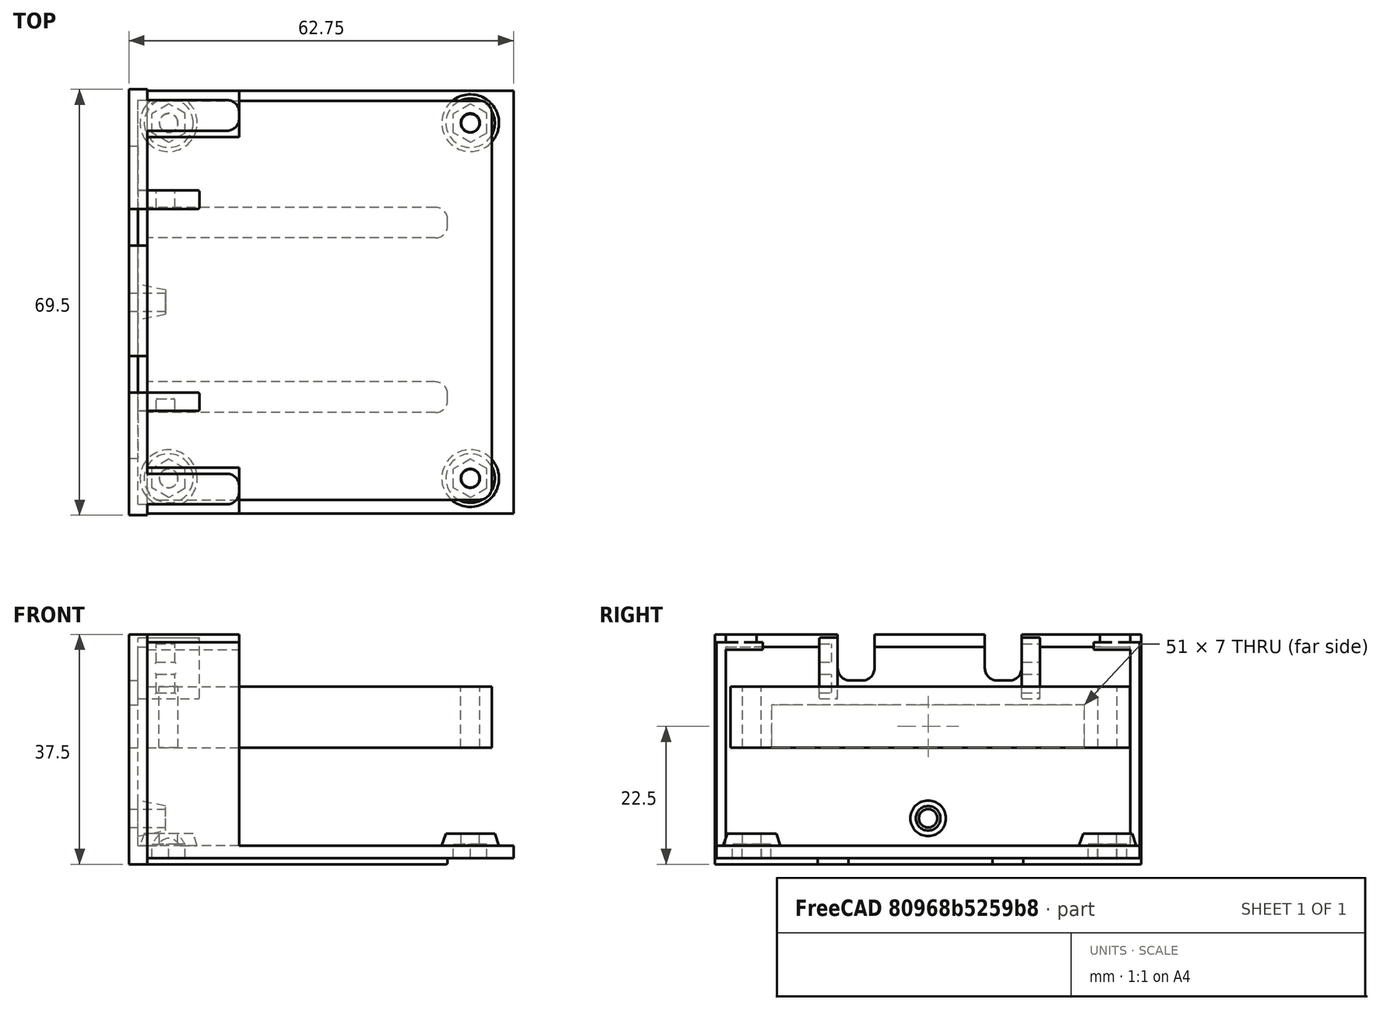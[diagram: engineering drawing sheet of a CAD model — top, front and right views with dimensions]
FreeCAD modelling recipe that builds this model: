
FCSTD DOCUMENT  (FreeCAD 0.19R24291 (Git))
Label: relay_tray
License: All rights reserved
LicenseURL: http://en.wikipedia.org/wiki/All_rights_reserved
objects: Part::Box×45, Part::MultiFuse×27, Part::Fillet×13, Part::Cut×10, Part::Cylinder×10, Part::Cone×6, Part::MultiCommon×4
note: 115 computed .brp shape members not serialized (recipe doc carries the construction recipe); baked Part::Feature solids carry a one-line shape summary decoded from their .brp

FEATURE [Part::Box] Box001  label="Cube"
  AttacherType = Attacher::AttachEngine3D
  Height = 37.5
  Length = 3
  Placement = pos=(-3,0,0) rot=(0,0,1;0rad)
  Width = 69.5
FEATURE [Part::Box] Box002  label="Cube001"
  AttacherType = Attacher::AttachEngine3D
  Height = 2
  Length = 60
  Placement = pos=(-0.25,0.25,1) rot=(0,0,1;0rad)
  Width = 69
FEATURE [Part::Box] Box003  label="Cube002"
  AttacherType = Attacher::AttachEngine3D
  Height = 34.75
  Length = 15
  Placement = pos=(0,0,2) rot=(0,0,1;0rad)
  Width = 7.5
FEATURE [Part::Box] Box004  label="Cube003"
  AttacherType = Attacher::AttachEngine3D
  Height = 34.75
  Length = 15
  Placement = pos=(0,61.5,2) rot=(0,0,1;0rad)
  Width = 7.5
FEATURE [Part::Box] Box005  label="Cube004"
  AttacherType = Attacher::AttachEngine3D
  Height = 34
  Length = 15
  Placement = pos=(0,1.5,1) rot=(0,0,1;0rad)
  Width = 7.5
FEATURE [Part::Box] Box006  label="Cube005"
  AttacherType = Attacher::AttachEngine3D
  Height = 34
  Length = 15
  Placement = pos=(0,60,1) rot=(0,0,1;0rad)
  Width = 7.5
FEATURE [Part::MultiFuse] Fusion001
  Shapes = -> [Box006,Box005]
FEATURE [Part::MultiFuse] Fusion002
  Placement = pos=(0,0,-0.5) rot=(0,0,1;0rad)
  Shapes = -> [Box004,Box003]
FEATURE [Part::Cut] Cut001
  Base = -> Fusion002
  Placement = pos=(0,0.25,0) rot=(0,0,1;0rad)
  Tool = -> Fusion001
FEATURE [Part::Box] Box007  label="Cube006"
  AttacherType = Attacher::AttachEngine3D
  Height = 32.5
  Length = 3.5
  Placement = pos=(-1.5,1.75,3) rot=(0,0,1;0rad)
  Width = 66
FEATURE [Part::Cut] Cut002
  Base = -> Box001
  Tool = -> Box007
FEATURE [Part::Cylinder] Cylinder004
  Angle = 360
  AttacherType = Attacher::AttachEngine3D
  Height = 10
  Placement = pos=(-5,6,32.5) rot=(0,1,0;1.5708rad)
  Radius = 1.5
FEATURE [Part::Cylinder] Cylinder005
  Angle = 360
  AttacherType = Attacher::AttachEngine3D
  Height = 10
  Placement = pos=(-5,6,32.5) rot=(0,1,0;1.5708rad)
  Radius = 1.5
FEATURE [Part::MultiFuse] Fusion003
  Placement = pos=(0,28.75,-25) rot=(0,0,1;0rad)
  Shapes = -> [Cylinder004,Cylinder005]
  expr: .Placement.Base.z = -25
FEATURE [Part::Box] Box008  label="Cube007"
  AttacherType = Attacher::AttachEngine3D
  Height = 7
  Length = 10
  Placement = pos=(-5,9.25,19) rot=(0,0,1;0rad)
  Width = 51
FEATURE [Part::Cone] Cone
  Angle = 360
  AttacherType = Attacher::AttachEngine3D
  Height = 5
  Placement = pos=(-1,6,32.5) rot=(0,1,0;1.5708rad)
  Radius1 = 3
  Radius2 = 2
FEATURE [Part::Cone] Cone001
  Angle = 360
  AttacherType = Attacher::AttachEngine3D
  Height = 5
  Placement = pos=(-1,6,32.5) rot=(0,1,0;1.5708rad)
  Radius1 = 3
  Radius2 = 2
FEATURE [Part::MultiFuse] Fusion004
  Placement = pos=(-1,28.75,-25) rot=(0,0,1;0rad)
  Shapes = -> [Cone,Cone001]
  expr: .Placement.Base.z = -25
FEATURE [Part::MultiFuse] Fusion005
  Shapes = -> [Cut002,Fusion004]
FEATURE [Part::Cut] Cut003
  Base = -> Fusion005
  Tool = -> Fusion003
FEATURE [Part::Cut] Cut004
  Base = -> Cut003
  Tool = -> Box008
FEATURE [Part::Cone] Cone002
  Angle = 360
  AttacherType = Attacher::AttachEngine3D
  Height = 3
  Placement = pos=(3.5,3.5,2) rot=(0,0,1;0rad)
  Radius1 = 5
  Radius2 = 4
FEATURE [Part::Box] Box014  label="Cube014"
  AttacherType = Attacher::AttachEngine3D
  Height = 5
  Length = 5.45
  Placement = pos=(3.25,0,0) rot=(0,0,1;0rad)
  Width = 10
FEATURE [Part::Box] Box015  label="Cube015"
  AttacherType = Attacher::AttachEngine3D
  Height = 5
  Length = 5.45
  Placement = pos=(11.5,4,0) rot=(0,0,1;2.0944rad)
  Width = 10
FEATURE [Part::Box] Box016  label="Cube016"
  AttacherType = Attacher::AttachEngine3D
  Height = 5
  Length = 10
  Placement = pos=(0.55,4,0) rot=(0,0,-1;0.523599rad)
  Width = 5.45
FEATURE [Part::Cylinder] Cylinder006
  Angle = 360
  AttacherType = Attacher::AttachEngine3D
  Height = 10
  Placement = pos=(4,4,-1) rot=(0,0,1;0rad)
  Radius = 1.5
FEATURE [Part::MultiCommon] Common  label="M.25 nut"
  Placement = pos=(-2,0,-1) rot=(0,0,1;0rad)
  Shapes = -> [Box014,Box016,Box015]
FEATURE [Part::MultiFuse] Fusion008  label="screw_hole"
  Placement = pos=(-0.5,-0.5,0) rot=(0,0,1;0rad)
  Shapes = -> [Cylinder006,Common]
FEATURE [Part::Cone] Cone003
  Angle = 360
  AttacherType = Attacher::AttachEngine3D
  Height = 3
  Placement = pos=(3.5,61.52,2) rot=(0,0,1;0rad)
  Radius1 = 5
  Radius2 = 4
FEATURE [Part::Cone] Cone004
  Angle = 360
  AttacherType = Attacher::AttachEngine3D
  Height = 3
  Placement = pos=(52.71,3.5,2) rot=(0,0,1;0rad)
  Radius1 = 5
  Radius2 = 4
FEATURE [Part::Cone] Cone005
  Angle = 360
  AttacherType = Attacher::AttachEngine3D
  Height = 3
  Placement = pos=(52.71,61.52,2) rot=(0,0,1;0rad)
  Radius1 = 5
  Radius2 = 4
FEATURE [Part::Box] Box017  label="Cube017"
  AttacherType = Attacher::AttachEngine3D
  Height = 5
  Length = 5.45
  Placement = pos=(3.25,0,0) rot=(0,0,1;0rad)
  Width = 10
FEATURE [Part::Box] Box018  label="Cube018"
  AttacherType = Attacher::AttachEngine3D
  Height = 5
  Length = 5.45
  Placement = pos=(11.5,4,0) rot=(0,0,1;2.0944rad)
  Width = 10
FEATURE [Part::Cylinder] Cylinder007
  Angle = 360
  AttacherType = Attacher::AttachEngine3D
  Height = 10
  Placement = pos=(4,4,-1) rot=(0,0,1;0rad)
  Radius = 1.5
FEATURE [Part::Box] Box019  label="Cube019"
  AttacherType = Attacher::AttachEngine3D
  Height = 5
  Length = 10
  Placement = pos=(0.55,4,0) rot=(0,0,-1;0.523599rad)
  Width = 5.45
FEATURE [Part::MultiCommon] Common001  label="M.25 nut001"
  Placement = pos=(-2,0,-1) rot=(0,0,1;0rad)
  Shapes = -> [Box017,Box019,Box018]
FEATURE [Part::MultiFuse] Fusion009  label="screw_hole001"
  Placement = pos=(-0.5,57.5,0) rot=(0,0,1;0rad)
  Shapes = -> [Cylinder007,Common001]
FEATURE [Part::Box] Box020  label="Cube020"
  AttacherType = Attacher::AttachEngine3D
  Height = 5
  Length = 5.45
  Placement = pos=(3.25,0,0) rot=(0,0,1;0rad)
  Width = 10
FEATURE [Part::Box] Box021  label="Cube021"
  AttacherType = Attacher::AttachEngine3D
  Height = 5
  Length = 5.45
  Placement = pos=(11.5,4,0) rot=(0,0,1;2.0944rad)
  Width = 10
FEATURE [Part::Cylinder] Cylinder008
  Angle = 360
  AttacherType = Attacher::AttachEngine3D
  Height = 10
  Placement = pos=(4,4,-1) rot=(0,0,1;0rad)
  Radius = 1.5
FEATURE [Part::Box] Box022  label="Cube022"
  AttacherType = Attacher::AttachEngine3D
  Height = 5
  Length = 10
  Placement = pos=(0.55,4,0) rot=(0,0,-1;0.523599rad)
  Width = 5.45
FEATURE [Part::MultiCommon] Common002  label="M.25 nut002"
  Placement = pos=(-2,0,-1) rot=(0,0,1;0rad)
  Shapes = -> [Box020,Box022,Box021]
FEATURE [Part::MultiFuse] Fusion010  label="screw_hole002"
  Placement = pos=(48.71,-0.5,0) rot=(0,0,1;0rad)
  Shapes = -> [Cylinder008,Common002]
FEATURE [Part::Box] Box023  label="Cube023"
  AttacherType = Attacher::AttachEngine3D
  Height = 5
  Length = 5.45
  Placement = pos=(3.25,0,0) rot=(0,0,1;0rad)
  Width = 10
FEATURE [Part::Box] Box024  label="Cube024"
  AttacherType = Attacher::AttachEngine3D
  Height = 5
  Length = 5.45
  Placement = pos=(11.5,4,0) rot=(0,0,1;2.0944rad)
  Width = 10
FEATURE [Part::Cylinder] Cylinder009
  Angle = 360
  AttacherType = Attacher::AttachEngine3D
  Height = 10
  Placement = pos=(4,4,-1) rot=(0,0,1;0rad)
  Radius = 1.5
FEATURE [Part::Box] Box025  label="Cube025"
  AttacherType = Attacher::AttachEngine3D
  Height = 5
  Length = 10
  Placement = pos=(0.55,4,0) rot=(0,0,-1;0.523599rad)
  Width = 5.45
FEATURE [Part::MultiCommon] Common003  label="M.25 nut003"
  Placement = pos=(-2,0,-1) rot=(0,0,1;0rad)
  Shapes = -> [Box023,Box025,Box024]
FEATURE [Part::MultiFuse] Fusion011  label="screw_hole003"
  Placement = pos=(48.71,57.5,0) rot=(0,0,1;0rad)
  Shapes = -> [Cylinder009,Common003]
FEATURE [Part::MultiFuse] Fusion012  label="Screw holes cut"
  Placement = pos=(0,2.5,-0.7) rot=(0,0,1;0rad)
  Shapes = -> [Fusion008,Fusion009,Fusion010,Fusion011]
FEATURE [Part::MultiFuse] Fusion013  label="Cones"
  Placement = pos=(0,2.5,0) rot=(0,0,1;0rad)
  Shapes = -> [Cone002,Cone003,Cone004,Cone005]
FEATURE [Part::MultiFuse] Fusion014
  Shapes = -> [Fusion013,Cut004,Box002]
FEATURE [Part::Cut] Cut005
  Base = -> Fusion014
  Tool = -> Fusion012
FEATURE [Part::Box] Box026  label="Cube026"
  AttacherType = Attacher::AttachEngine3D
  Height = 15
  Length = 10
  Placement = pos=(0,0,16) rot=(0,0,1;0rad)
  Width = 6
FEATURE [Part::Fillet] Fillet012
  Base = -> Box026
  Edges = 2 edges r=2: [Edge9,Edge11]
  Placement = pos=(-4,20,7) rot=(0,0,1;0rad)
FEATURE [Part::Box] Box027  label="Cube027"
  AttacherType = Attacher::AttachEngine3D
  Height = 15
  Length = 10
  Placement = pos=(0,0,16) rot=(0,0,1;0rad)
  Width = 6
FEATURE [Part::Fillet] Fillet013
  Base = -> Box027
  Edges = 2 edges r=2: [Edge9,Edge11]
  Placement = pos=(-4,44,7) rot=(0,0,1;0rad)
FEATURE [Part::MultiFuse] Fusion016  label="Cables sockets"
  Placement = pos=(0,0,7) rot=(0,0,1;0rad)
  Shapes = -> [Fillet012,Fillet013]
FEATURE [Part::Box] Box028  label="Cube028"
  AttacherType = Attacher::AttachEngine3D
  Height = 2
  Length = 15
  Placement = pos=(0,-15.5,0) rot=(0,0,1;0rad)
  Width = 5
FEATURE [Part::Fillet] Fillet
  Base = -> Box028
  Edges = 2 edges r=2: [Edge5,Edge7]
  Placement = pos=(0,17,0) rot=(0,0,1;0rad)
FEATURE [Part::Box] Box029  label="Cube029"
  AttacherType = Attacher::AttachEngine3D
  Height = 2
  Length = 49
  Width = 5
FEATURE [Part::Fillet] Fillet014
  Base = -> Box029
  Edges = 2 edges r=2: [Edge5,Edge7]
  Placement = pos=(0,45,0) rot=(0,0,1;0rad)
FEATURE [Part::Fillet] Fillet015
  Base = -> Fillet
  Edges = 2 edges r=0.25: [Edge14,Edge16]
  Placement = pos=(0,0.25,35.5) rot=(0,0,1;0rad)
FEATURE [Part::Fillet] Fillet016
  Base = -> Fillet014
  Edges = 2 edges r=0.25: [Edge14,Edge16]
  Placement = pos=(0,0.25,0) rot=(0,0,1;0rad)
FEATURE [Part::Box] Box030  label="Cube030"
  AttacherType = Attacher::AttachEngine3D
  Height = 2
  Length = 49
  Width = 5
FEATURE [Part::Fillet] Fillet017
  Base = -> Box030
  Edges = 2 edges r=2: [Edge5,Edge7]
  Placement = pos=(0,17,0) rot=(0,0,1;0rad)
FEATURE [Part::Fillet] Fillet018
  Base = -> Fillet017
  Edges = 2 edges r=0.25: [Edge14,Edge16]
  Placement = pos=(0,-0.25,0) rot=(0,0,1;0rad)
FEATURE [Part::Box] Box031  label="Cube031"
  AttacherType = Attacher::AttachEngine3D
  Height = 2
  Length = 15
  Placement = pos=(0,-15.25,0) rot=(0,0,1;0rad)
  Width = 5
FEATURE [Part::Fillet] Fillet019
  Base = -> Box031
  Edges = 2 edges r=2: [Edge5,Edge7]
  Placement = pos=(0,17,0) rot=(0,0,1;0rad)
FEATURE [Part::Fillet] Fillet020
  Base = -> Fillet019
  Edges = 2 edges r=0.25: [Edge14,Edge16]
  Placement = pos=(0,61,35.5) rot=(0,0,1;0rad)
FEATURE [Part::MultiFuse] Fusion017  label="rails"
  Shapes = -> [Fillet015,Fillet016,Fillet018,Fillet020]
FEATURE [Part::MultiFuse] Fusion018  label="Arduino tray rough"
  Shapes = -> [Fusion017]
FEATURE [Part::Box] Box032  label="Cube032"
  AttacherType = Attacher::AttachEngine3D
  Height = 10
  Length = 10
  Placement = pos=(0,10,26) rot=(0,0,1;0rad)
  Width = 3
FEATURE [Part::Box] Box033  label="Cube033"
  AttacherType = Attacher::AttachEngine3D
  Height = 3
  Length = 3
  Placement = pos=(3,10,27) rot=(0,0,1;0rad)
  Width = 2
FEATURE [Part::Box] Box034  label="Cube034"
  AttacherType = Attacher::AttachEngine3D
  Height = 3
  Length = 3
  Placement = pos=(3,10,32) rot=(0,0,1;0rad)
  Width = 2
FEATURE [Part::MultiFuse] Fusion019
  Shapes = -> [Box033,Box034]
FEATURE [Part::Cut] Cut007
  Base = -> Box032
  Tool = -> Fusion019
FEATURE [Part::Fillet] Fillet022  label="zip ties holder"
  Base = -> Cut007
  Edges = 22 edges r=0.2: [Edge5,Edge6,Edge7,Edge8,Edge9,Edge10,Edge11,Edge12,Edge13,Edge14,Edge15,Edge16,Edge19,Edge20,Edge21,Edge22,Edge23,Edge24,Edge25,Edge26,Edge27,Edge28]
  Placement = pos=(-1,0,-1) rot=(0,0,1;0rad)
FEATURE [Part::Box] Box035  label="Cube035"
  AttacherType = Attacher::AttachEngine3D
  Height = 10
  Length = 10
  Placement = pos=(0,16,26) rot=(0,0,1;0rad)
  Width = 3
FEATURE [Part::Box] Box036  label="Cube036"
  AttacherType = Attacher::AttachEngine3D
  Height = 3
  Length = 3
  Placement = pos=(3,16,27) rot=(0,0,1;0rad)
  Width = 3
FEATURE [Part::Box] Box037  label="Cube037"
  AttacherType = Attacher::AttachEngine3D
  Height = 3
  Length = 3
  Placement = pos=(3,16,32) rot=(0,0,1;0rad)
  Width = 3
FEATURE [Part::MultiFuse] Fusion020
  Shapes = -> [Box036,Box037]
FEATURE [Part::Cut] Cut008
  Base = -> Box035
  Tool = -> Fusion020
FEATURE [Part::Fillet] Fillet023  label="zip ties holder001"
  Base = -> Cut008
  Edges = 22 edges r=0.2: [Edge5,Edge6,Edge7,Edge8,Edge9,Edge10,Edge11,Edge12,Edge13,Edge14,Edge15,Edge16,Edge19,Edge20,Edge21,Edge22,Edge23,Edge24,Edge25,Edge26,Edge27,Edge28]
  Placement = pos=(-1,27,-1) rot=(0,0,1;0rad)
FEATURE [Part::MultiFuse] Fusion021  label="zip ties holders"
  Placement = pos=(-0.5,7,2) rot=(0,0,1;0rad)
  Shapes = -> [Fillet022,Fillet023]
FEATURE [Part::MultiFuse] Fusion015
  Shapes = -> [Cut005,Cut001,Fusion021]
FEATURE [Part::Box] Box038  label="Cube038"
  AttacherType = Attacher::AttachEngine3D
  Height = 10
  Length = 5
  Placement = pos=(21,2,-3) rot=(0,0,1;0rad)
  Width = 2
FEATURE [Part::Box] Box039  label="Cube039"
  AttacherType = Attacher::AttachEngine3D
  Height = 10
  Length = 5
  Placement = pos=(30,2,-3) rot=(0,0,1;0rad)
  Width = 2
FEATURE [Part::Box] Box040  label="Cube040"
  AttacherType = Attacher::AttachEngine3D
  Height = 10
  Length = 5
  Placement = pos=(39,2,-3) rot=(0,0,1;0rad)
  Width = 2
FEATURE [Part::MultiFuse] Fusion022  label="zip ties holes board r"
  Shapes = -> [Box038,Box039,Box040]
FEATURE [Part::Box] Box041  label="Cube041"
  AttacherType = Attacher::AttachEngine3D
  Height = 10
  Length = 5
  Placement = pos=(21,2,-3) rot=(0,0,1;0rad)
  Width = 2
FEATURE [Part::Box] Box042  label="Cube042"
  AttacherType = Attacher::AttachEngine3D
  Height = 10
  Length = 5
  Placement = pos=(30,2,-3) rot=(0,0,1;0rad)
  Width = 2
FEATURE [Part::Box] Box043  label="Cube043"
  AttacherType = Attacher::AttachEngine3D
  Height = 10
  Length = 5
  Placement = pos=(39,2,-3) rot=(0,0,1;0rad)
  Width = 2
FEATURE [Part::MultiFuse] Fusion023  label="zip ties holes board l"
  Placement = pos=(0,64,0) rot=(0,0,1;0rad)
  Shapes = -> [Box041,Box042,Box043]
FEATURE [Part::Box] Box044  label="Cube044"
  AttacherType = Attacher::AttachEngine3D
  Height = 10
  Length = 5
  Placement = pos=(21,2,-3) rot=(0,0,1;0rad)
  Width = 2
FEATURE [Part::Box] Box045  label="Cube045"
  AttacherType = Attacher::AttachEngine3D
  Height = 10
  Length = 5
  Placement = pos=(30,2,-3) rot=(0,0,1;0rad)
  Width = 2
FEATURE [Part::Box] Box046  label="Cube046"
  AttacherType = Attacher::AttachEngine3D
  Height = 10
  Length = 5
  Placement = pos=(39,2,-3) rot=(0,0,1;0rad)
  Width = 2
FEATURE [Part::MultiFuse] Fusion024  label="zip ties holes board r001"
  Placement = pos=(0,4,0) rot=(0,0,1;0rad)
  Shapes = -> [Box044,Box045,Box046]
FEATURE [Part::Box] Box047  label="Cube047"
  AttacherType = Attacher::AttachEngine3D
  Height = 10
  Length = 5
  Placement = pos=(21,2,-3) rot=(0,0,1;0rad)
  Width = 2
FEATURE [Part::Box] Box048  label="Cube048"
  AttacherType = Attacher::AttachEngine3D
  Height = 10
  Length = 5
  Placement = pos=(30,2,-3) rot=(0,0,1;0rad)
  Width = 2
FEATURE [Part::Box] Box049  label="Cube049"
  AttacherType = Attacher::AttachEngine3D
  Height = 10
  Length = 5
  Placement = pos=(39,2,-3) rot=(0,0,1;0rad)
  Width = 2
FEATURE [Part::MultiFuse] Fusion025  label="zip ties holes board l001"
  Placement = pos=(0,60,0) rot=(0,0,1;0rad)
  Shapes = -> [Box047,Box048,Box049]
FEATURE [Part::MultiFuse] Fusion026  label="zip ties holes"
  Shapes = -> [Fusion022,Fusion023,Fusion024,Fusion025]
FEATURE [Part::MultiFuse] Fusion027  label="Cable holders"
FEATURE [Part::Box] Box  label="Cube050"
  AttacherType = Attacher::AttachEngine3D
  Height = 10
  Length = 56.21
  Width = 65.15
FEATURE [Part::Fillet] Fillet024
  Base = -> Box
  Edges = 4 edges r=2: [Edge1,Edge3,Edge5,Edge7]
FEATURE [Part::Cylinder] Cylinder
  Angle = 360
  AttacherType = Attacher::AttachEngine3D
  Height = 10
  Placement = pos=(3.5,3.5,0) rot=(0,0,1;0rad)
  Radius = 1.55
FEATURE [Part::Cylinder] Cylinder010
  Angle = 360
  AttacherType = Attacher::AttachEngine3D
  Height = 10
  Placement = pos=(3.5,61.52,0) rot=(0,0,1;0rad)
  Radius = 1.55
FEATURE [Part::Cylinder] Cylinder011
  Angle = 360
  AttacherType = Attacher::AttachEngine3D
  Height = 10
  Placement = pos=(52.71,3.5,0) rot=(0,0,1;0rad)
  Radius = 1.55
FEATURE [Part::Cylinder] Cylinder012
  Angle = 360
  AttacherType = Attacher::AttachEngine3D
  Height = 10
  Placement = pos=(52.71,61.52,0) rot=(0,0,1;0rad)
  Radius = 1.55
FEATURE [Part::MultiFuse] Fusion  label="Fusion - holes"
  Shapes = -> [Cylinder,Cylinder010,Cylinder011,Cylinder012]
FEATURE [Part::Cut] Cut  label="board"
  Base = -> Fillet024
  Placement = pos=(0,2.5,19) rot=(0,0,1;0rad)
  Tool = -> Fusion
FEATURE [Part::Cut] Cut009
  Base = -> Fusion018
  Tool = -> Fusion026
FEATURE [Part::MultiFuse] Fusion028  label="Relay_tray1"
  Shapes = -> [Fusion015,Cut009]
FEATURE [Part::Cut] Cut010  label="Relay_tray"
  Base = -> Fusion028
  Tool = -> Fusion016
